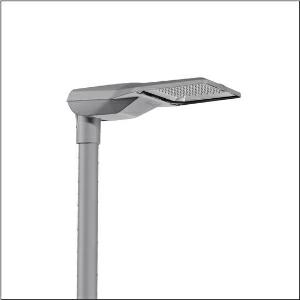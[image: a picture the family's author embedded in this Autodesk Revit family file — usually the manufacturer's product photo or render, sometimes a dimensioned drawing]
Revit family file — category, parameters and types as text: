
# Revit family: streetlight_sl_21_iq_midi___p0_8a_5xe3u31g08mb_ba97
name_source: partatom
category: Lighting Fixtures
units: mm (PartAtom-declared; Revit-internal decimal feet)

## family parameters
Cut with Voids When Loaded = No
Host = Face
Light Source = No
Part Type = Normal
Room Calculation Point = No
Round Connector Dimension = Use Diameter
Shared = No

## types (1)
- --- (1 x LED, 19670 lm, 146.7 W, 3000K)
    Apparent Load = 147 VA
    CIE Flux Codes = 33 69 96 100 100
    Color Rendering = 70
    Color Temperature = 3000K
    Default Elevation = 1800 mm
    Description = Streetlight SL 21 iQ midi, mast luminaire, primary light control with lens, of PMMA, primary optical cover: cover, of toughened safety glass, transparent, light distribution: P0.8a, light emission: direct distribution, primary light characteristic: asymmetric, installation type: post-top, side-entry, LED, High Power LED, rated luminous flux: 19.670lm, luminous efficacy: 134lm/W, light colour: 730, colour temperature: 3000K, control gear: iQ Street-Remote, control: pre-setting: linear dimming characteristic, Street-Remote, Auto-Match, Temp-Guard, Lumen-Switch, Night-Set, Smart-Wire, Light-Fading, Desk-Remote (wireless, voltage-free reading and setting of iQ features in the workshop via application-optimized NFC function/RFID function), optimised constant luminous flux control (CLO 2.0), mains connection: 230..240V, AC, 50/60Hz, start of lifetime: 147W, end of service life: 161W, reduction: 62W, luminaire housing, of diecast aluminium, powder-coated, Siteco® metallic grey (DB 702S), corrosivity category C5 high according to DIN EN ISO 12944, please order mast flange separately, inclination adjustable: 0°, 5°, 10°, 15°, sealing non-destructively replaceable, multi-level sealing system, length: 644mm, width: 335mm, height: 110mm, mast flange for spigot size: 42mm (side-entry): 5XC10008XM4, 60/48mm (side-entry/post-top): 5XC10108XM2, 76/60mm (side-entry/post-top): 5XC10108XM1, mounting height: 4..8m, protection rating (complete): IP66, insulation class (complete): insulation class II (safety insulation), certification: CE, ENEC, ENEC+, VDE, impact resistance: IK10, permissible operating ambient temperature for outdoor applications: -40..+50°C, standard-compliant lighting for roads and squares, packaging unit: 1 piece

Light Distribution: P0.8a
    Height = 111 mm
    Lamp = 1 x LED
    Lamp Light Flux = 19670 lm
    Lamp Power = 146.7 W
    Lamp count = 1
    Length = 644 mm
    Luminous efficacy = 134 lm/W
    Manufacturer = Siteco
    ModVariant = No
    Model = 5XE3U31G08MB
    Number of Poles = 1
    OnlyDefault = Yes
    Power Factor = 1
    Product Name = Streetlight SL 21 iQ midi | P0.8a
    Product group = mast luminaire | pylon top
    ProductGroupID = 6100
    Protection Class = Protection class II
    Protection Degree = IP 66
    RLX_Detail_Level = 1
    RLX_Emergency_Light_Flux = 0 lm
    RLX_Emergency_Type = 0
    RLX_Emergency_Type_DB = No
    RlxData = <blob elided: 90533 chars, md5=49e837ee>
    Socket = socket
    Standby Power = 0 W
    System Light Flux = 19670 lm
    System Power = 147 W
    Type Comments = factory setting: luminous flux: 100 % | dim-lin: 254 | 753 mA
    Type Image = l_1004298.jpg
    URL = http://relux.com
    VarID = @adj_082745
    Voltage = 0 V
    Weight = 0.00 kg
    Width = 336 mm

## geometry (parser evidence)
native form markers: Blend x4, Sweep x12
no freeform markers — native parametric forms only
